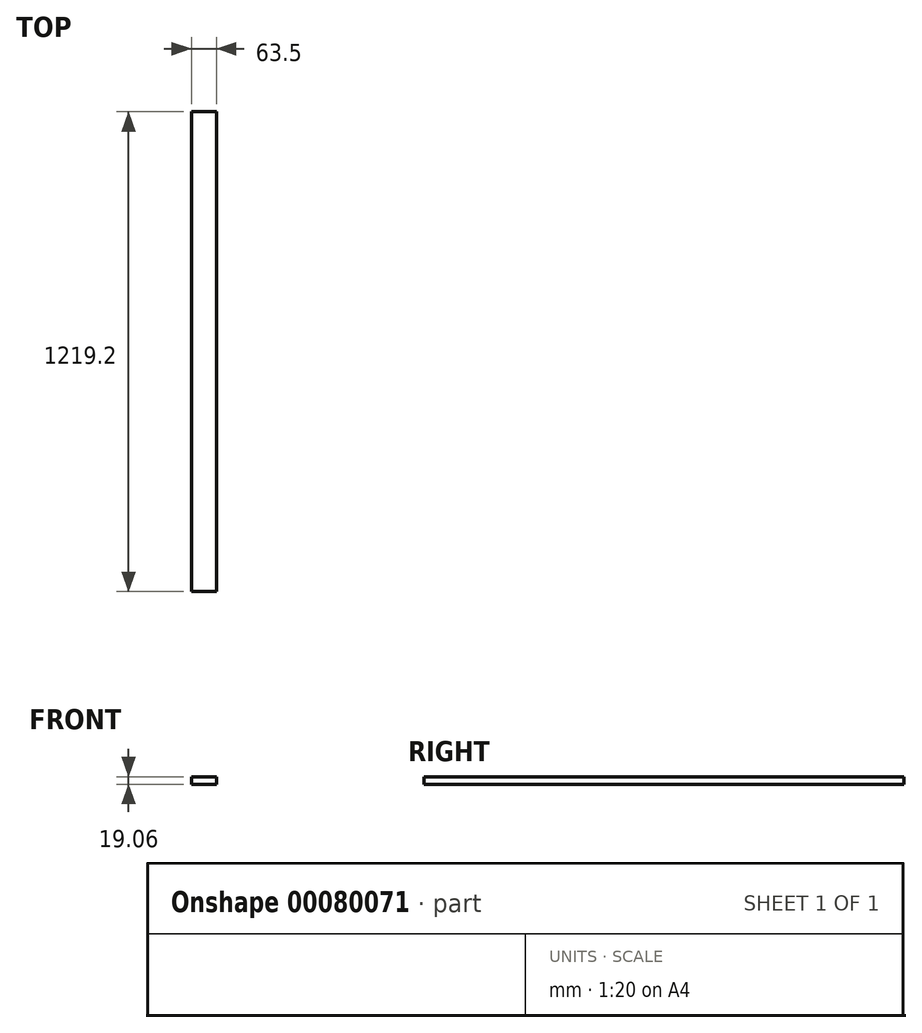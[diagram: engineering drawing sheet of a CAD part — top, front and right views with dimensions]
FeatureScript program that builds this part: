
annotation { "Feature Type Name" : "Feature", "Feature Type Description" : "" }
export const myFeature = defineFeature(function(context is Context, id is Id, definition is map)
    precondition{}
    {
        {
            var Q0;
            Q0=qCreatedBy(makeId("Front.planeOp"),FACE);
            var sketch = newSketch(context, id + "F0", { "sketchPlane" : qUnion([Q0])});
            skLineSegment(sketch, "E0.bottom", {"start": v(-31.75, 9.53) * mm, "end": v(31.75, 9.53) * mm});
            skLineSegment(sketch, "E0.top", {"start": v(-31.75, -9.52) * mm, "end": v(31.75, -9.52) * mm});
            skLineSegment(sketch, "E0.left", {"start": v(-31.75, 9.53) * mm, "end": v(-31.75, -9.52) * mm});
            skLineSegment(sketch, "E0.right", {"start": v(31.75, 9.53) * mm, "end": v(31.75, -9.52) * mm});
            skPoint(sketch, "E0.middle", {"position": v(0, 0) * mm});
            skSolve(sketch);
        }
        {
            var Q0;
            Q0 = qSketchRegion(id + "F0", true);
            extrude(context, id + "F1", {"entities" : qUnion([Q0]), "endBound" : BoundingType.SYMMETRIC, "depth" : 1219.2 * mm});
        }
    });
